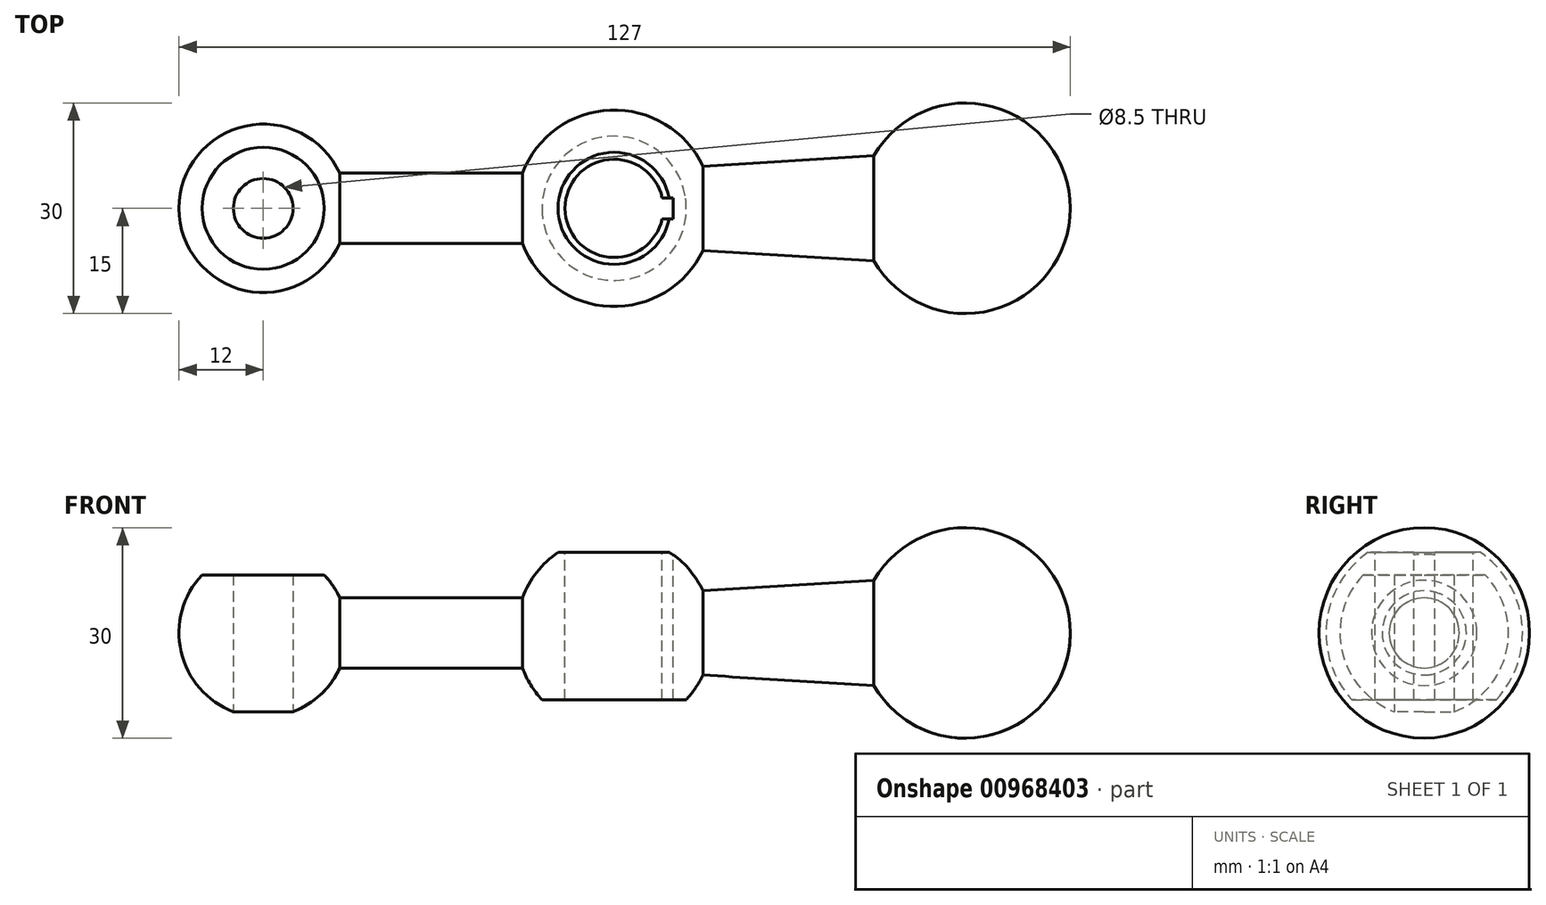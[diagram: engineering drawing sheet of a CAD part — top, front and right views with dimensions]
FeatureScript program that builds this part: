
annotation { "Feature Type Name" : "Feature", "Feature Type Description" : "" }
export const myFeature = defineFeature(function(context is Context, id is Id, definition is map)
    precondition{}
    {
        {
            var Q0;
            Q0=qCreatedBy(makeId("Front.planeOp"),FACE);
            var sketch = newSketch(context, id + "F0", { "sketchPlane" : qUnion([Q0])});
            skCircle(sketch, "E0", {"center": v(0, 0) * mm, "radius": 15 * mm});
            skArc(sketch, "E1", {"start": v(-39.72, -9.5) * mm, "mid": v(-36.08, 1.52) * mm, "end": v(-42.02, 11.5) * mm});
            skArc(sketch, "E2", {"start": v(-108.7, 8.26) * mm, "mid": v(-100, -12) * mm, "end": v(-91.3, 8.26) * mm});
            skLineSegment(sketch, "E3", {"start": v(-37.35, 6) * mm, "end": v(-13, 7.5) * mm});
            skLineSegment(sketch, "E4", {"start": v(-37.35, -6) * mm, "end": v(-13, -7.5) * mm});
            skLineSegment(sketch, "E5", {"start": v(-89.1, 5) * mm, "end": v(-63.08, 5) * mm});
            skLineSegment(sketch, "E6", {"start": v(-89.1, -5) * mm, "end": v(-63.08, -5) * mm});
            skLineSegment(sketch, "E7", {"start": v(-108.7, 8.26) * mm, "end": v(-91.3, 8.26) * mm});
            skLineSegment(sketch, "E8", {"start": v(-60.28, -9.5) * mm, "end": v(-39.72, -9.5) * mm});
            skLineSegment(sketch, "E9", {"start": v(-100, 8.26) * mm, "end": v(-100, -12) * mm});
            skLineSegment(sketch, "E10", {"start": v(-50, -9.5) * mm, "end": v(-50, 11.5) * mm});
            skLineSegment(sketch, "E11", {"start": v(15, 0) * mm, "end": v(-36, 0) * mm});
            skLineSegment(sketch, "E12", {"start": v(-88, 0) * mm, "end": v(-64, 0) * mm});
            skLineSegment(sketch, "E13", {"start": v(-57.98, 11.5) * mm, "end": v(-42.02, 11.5) * mm});
            skArc(sketch, "E14.trimOffspring", {"start": v(-57.98, 11.5) * mm, "mid": v(-63.92, 1.52) * mm, "end": v(-60.28, -9.5) * mm});
            skSolve(sketch);
        }
        {
            var Q0;
            Q0=qCreatedBy(makeId("Top.planeOp"),FACE);
            var sketch = newSketch(context, id + "F1", { "sketchPlane" : qUnion([Q0])});
            skArc(sketch, "E15", {"start": v(-43.16, 1.5) * mm, "mid": v(-57, 0) * mm, "end": v(-43.16, -1.5) * mm});
            skLineSegment(sketch, "E16", {"start": v(-43.16, 1.5) * mm, "end": v(-41.6, 1.5) * mm});
            skLineSegment(sketch, "E17", {"start": v(-41.6, 1.5) * mm, "end": v(-41.6, -1.5) * mm});
            skLineSegment(sketch, "E18", {"start": v(-41.6, -1.5) * mm, "end": v(-43.16, -1.5) * mm});
            skSolve(sketch);
        }
        {
            var Q0;
            {var subQ0=sQuery(id+"F0.wireOp",EDGE,"E0");var subQ1=makeQuery(id+"F0.imprint","INTERSECT",VERTEX,{"derivedFrom":[subQ0,sQuery(id+"F0.wireOp",EDGE,"E3")]});Q0=makeQuery(id+"F0.imprint","IMPRINT",FACE,{"disambiguationData":[TD([[makeQuery(id+"F0.imprint","IMPRINT",EDGE,{"disambiguationData":[TD([[subQ1,1.0]])],"derivedFrom":subQ0}),1.0]])]});}
            var Q1;
            {var subQ0=sQuery(id+"F0.wireOp",EDGE,"E3");Q1=makeQuery(id+"F0.imprint","IMPRINT",FACE,{"disambiguationData":[TD([[makeQuery(id+"F0.imprint","IMPRINT",EDGE,{"derivedFrom":subQ0}),-1.0]])]});}
            var Q2;
            Q2=sQuery(id+"F0.wireOp",EDGE,"E11");
            revolve(context, id + "F2", {"surfaceOperationType" : NewSurfaceOperationType.NEW, "entities" : qUnion([Q0, Q1]), "axis" : qUnion([Q2]), "revolveType" : RevolveType.FULL});
        }
        {
            var Q0;
            {var subQ2=sQuery(id+"F0.wireOp",EDGE,"E10");Q0=makeQuery(id+"F0.imprint","IMPRINT",FACE,{"disambiguationData":[TD([[makeQuery(id+"F0.imprint","IMPRINT",EDGE,{"derivedFrom":subQ2}),-1.0]])]});}
            var Q1;
            Q1=sQuery(id+"F0.wireOp",EDGE,"E10");
            revolve(context, id + "F3", {"operationType" : NewBodyOperationType.ADD, "surfaceOperationType" : NewSurfaceOperationType.NEW, "entities" : qUnion([Q0]), "axis" : qUnion([Q1]), "revolveType" : RevolveType.FULL});
        }
        {
            var Q0;
            {var subQ0=sQuery(id+"F0.wireOp",EDGE,"E5");Q0=makeQuery(id+"F0.imprint","IMPRINT",FACE,{"disambiguationData":[TD([[makeQuery(id+"F0.imprint","IMPRINT",EDGE,{"derivedFrom":subQ0}),-1.0]])]});}
            var Q1;
            Q1=sQuery(id+"F0.wireOp",EDGE,"E12");
            revolve(context, id + "F4", {"operationType" : NewBodyOperationType.ADD, "surfaceOperationType" : NewSurfaceOperationType.NEW, "entities" : qUnion([Q0]), "axis" : qUnion([Q1]), "revolveType" : RevolveType.FULL});
        }
        {
            var Q0;
            {var subQ6=sQuery(id+"F0.wireOp",EDGE,"E9");Q0=makeQuery(id+"F0.imprint","IMPRINT",FACE,{"disambiguationData":[TD([[makeQuery(id+"F0.imprint","IMPRINT",EDGE,{"derivedFrom":subQ6}),1.0]])]});}
            var Q1;
            Q1=sQuery(id+"F0.wireOp",EDGE,"E9");
            revolve(context, id + "F5", {"operationType" : NewBodyOperationType.ADD, "surfaceOperationType" : NewSurfaceOperationType.NEW, "entities" : qUnion([Q0]), "axis" : qUnion([Q1]), "revolveType" : RevolveType.FULL});
        }
        {
            var Q0;
            Q0=makeQuery(id+"F1.imprint","IMPRINT",FACE,{"disambiguationData":[TD([[makeQuery(id+"F1.imprint","IMPRINT",EDGE,{"derivedFrom":sQuery(id+"F1.wireOp",EDGE,"E15")}),1.0]])]});
            extrude(context, id + "F6", {"entities" : qUnion([Q0]), "operationType" : NewBodyOperationType.REMOVE, "oppositeDirection" : true, "depth" : 30 * mm, "offsetDistance" : 25 * mm, "symmetric" : true});
        }
        {
            var Q0;
            Q0=makeQuery(id+"F5.opRevolve","SWEPT_FACE",FACE,{"disambiguationData":[OSD([sQuery(id+"F0.wireOp",EDGE,"E7")])]});
            var sketch = newSketch(context, id + "F7", { "sketchPlane" : qUnion([Q0])});
            skPoint(sketch, "E19.0", {"position": v(-100, 0) * mm});
            skSolve(sketch);
        }
        {
            var Q0;
            Q0=sQuery(id+"F7.wireOp",VERTEX,"E19.0");
            var Q1;
            Q1=makeQuery(id+"F2.opRevolve","SWEPT_BODY",BODY,{"disambiguationData":[OSD([sQuery(id+"F0.wireOp",EDGE,"E0"),sQuery(id+"F0.wireOp",EDGE,"E1"),sQuery(id+"F0.wireOp",EDGE,"E3"),sQuery(id+"F0.wireOp",EDGE,"E11")])]});
            hole(context, id + "F8", {"style" : HoleStyle.SIMPLE, "endStyle" : HoleEndStyle.THROUGH, "standardTappedOrClearance" : lookupTablePath({ "standard" : "ISO", "engagement" : "75%", "pitch" : "1.5 mm", "size" : "M10", "type" : "Tapped" }), "standardBlindInLast" : lookupTablePath({ "standard" : "ISO", "fit" : "Normal", "engagement" : "75%", "pitch" : "1.5 mm", "size" : "M10", "type" : "Clearance & tapped" }), "holeDiameter" : 8.5 * mm, "majorDiameter" : 10 * mm, "showTappedDepth" : true, "isTappedThrough" : true, "tappedDepth" : 14 * mm, "tapClearance" : 0, "startFromSketch" : true, "locations" : qUnion([Q0]), "scope" : qUnion([Q1])});
        }
    });
